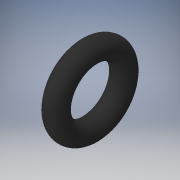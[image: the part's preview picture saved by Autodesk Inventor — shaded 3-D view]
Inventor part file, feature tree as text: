
AUTODESK INVENTOR PART (.ipt)
format: ipt  version: 2018 (Build 220112000, 112)  size: 145,408 bytes
history: native  units: in
note: dims shown in document units (in); Inventor stores cm internally (conversion verified against a paired STEP export)
features: revolve x1, sketch x1
ambient origin geometry x8: Origin, YZ Plane, XZ Plane, XY Plane, X Axis, Y Axis, Z Axis, Center Point
bodies: Solid1 (feature_tree)
feature tree (2):
  revolve  "Revolution1"  [1 undecoded]
  sketch  "Sketch1"  dims[d1=0.139in d2=0.1562in d3=90.0deg]
note: 1 required parameter value undecoded (feature->parameter linkage not recoverable at this tier; creation-order binding heuristic only, values carry confidence <= 0.55)
